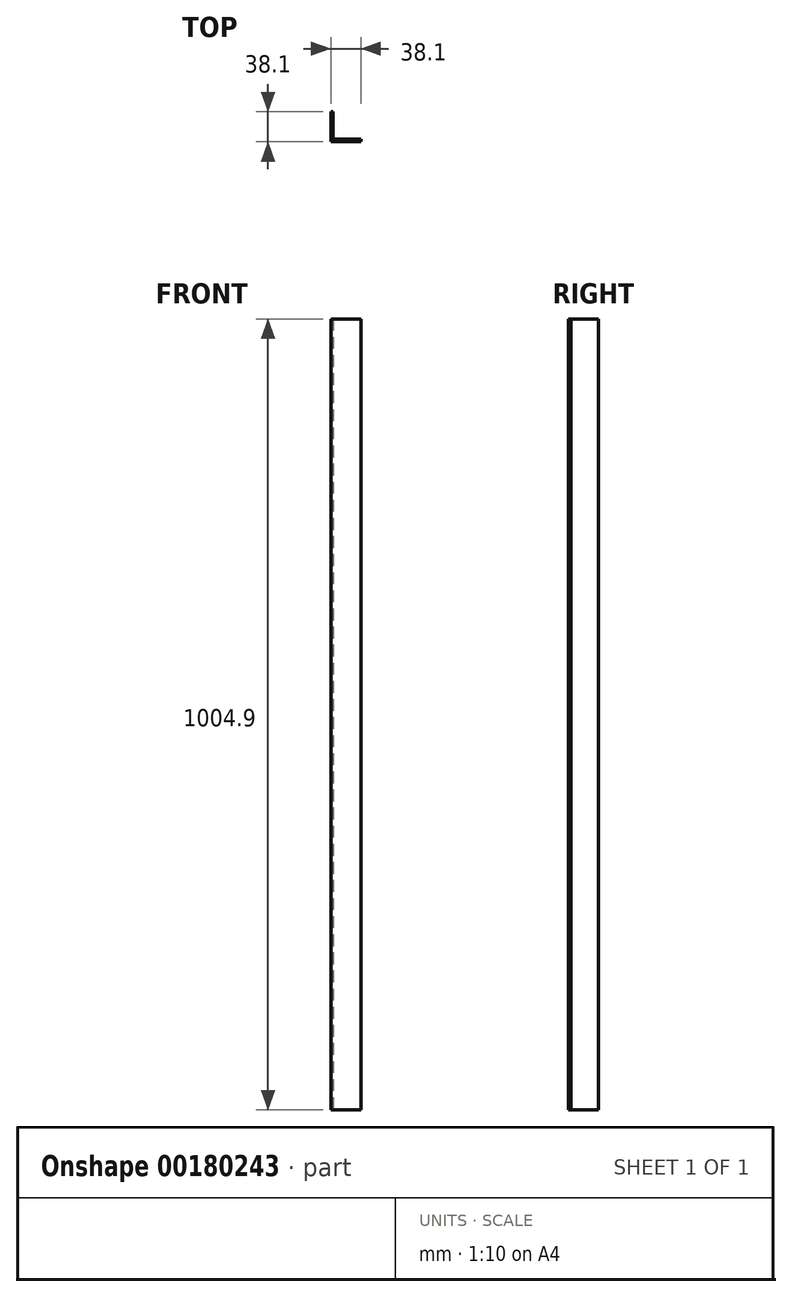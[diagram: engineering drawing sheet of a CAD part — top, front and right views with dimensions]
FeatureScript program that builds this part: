
annotation { "Feature Type Name" : "Feature", "Feature Type Description" : "" }
export const myFeature = defineFeature(function(context is Context, id is Id, definition is map)
    precondition{}
    {
        {
            var Q0;
            Q0=qCreatedBy(makeId("Top.planeOp"),FACE);
            var sketch = newSketch(context, id + "F0", { "sketchPlane" : qUnion([Q0])});
            skLineSegment(sketch, "E0", {"start": v(0, 0) * mm, "end": v(38.1, 0) * mm});
            skLineSegment(sketch, "E1", {"start": v(0, 0) * mm, "end": v(0, 38.1) * mm});
            skLineSegment(sketch, "E2.0", {"start": v(3, 3) * mm, "end": v(3, 38.1) * mm});
            skLineSegment(sketch, "E2.1", {"start": v(3, 3) * mm, "end": v(38.1, 3) * mm});
            skLineSegment(sketch, "E3", {"start": v(38.1, 3) * mm, "end": v(38.1, 0) * mm});
            skLineSegment(sketch, "E4", {"start": v(0, 38.1) * mm, "end": v(3, 38.1) * mm});
            skSolve(sketch);
        }
        {
            var Q0;
            Q0=makeQuery(id+"F0.imprint","IMPRINT",FACE,{"disambiguationData":[TD([[makeQuery(id+"F0.imprint","IMPRINT",EDGE,{"derivedFrom":sQuery(id+"F0.wireOp",EDGE,"E0")}),1.0]])]});
            extrude(context, id + "F1", {"entities" : qUnion([Q0]), "depth" : 1004.9 * mm});
        }
    });
